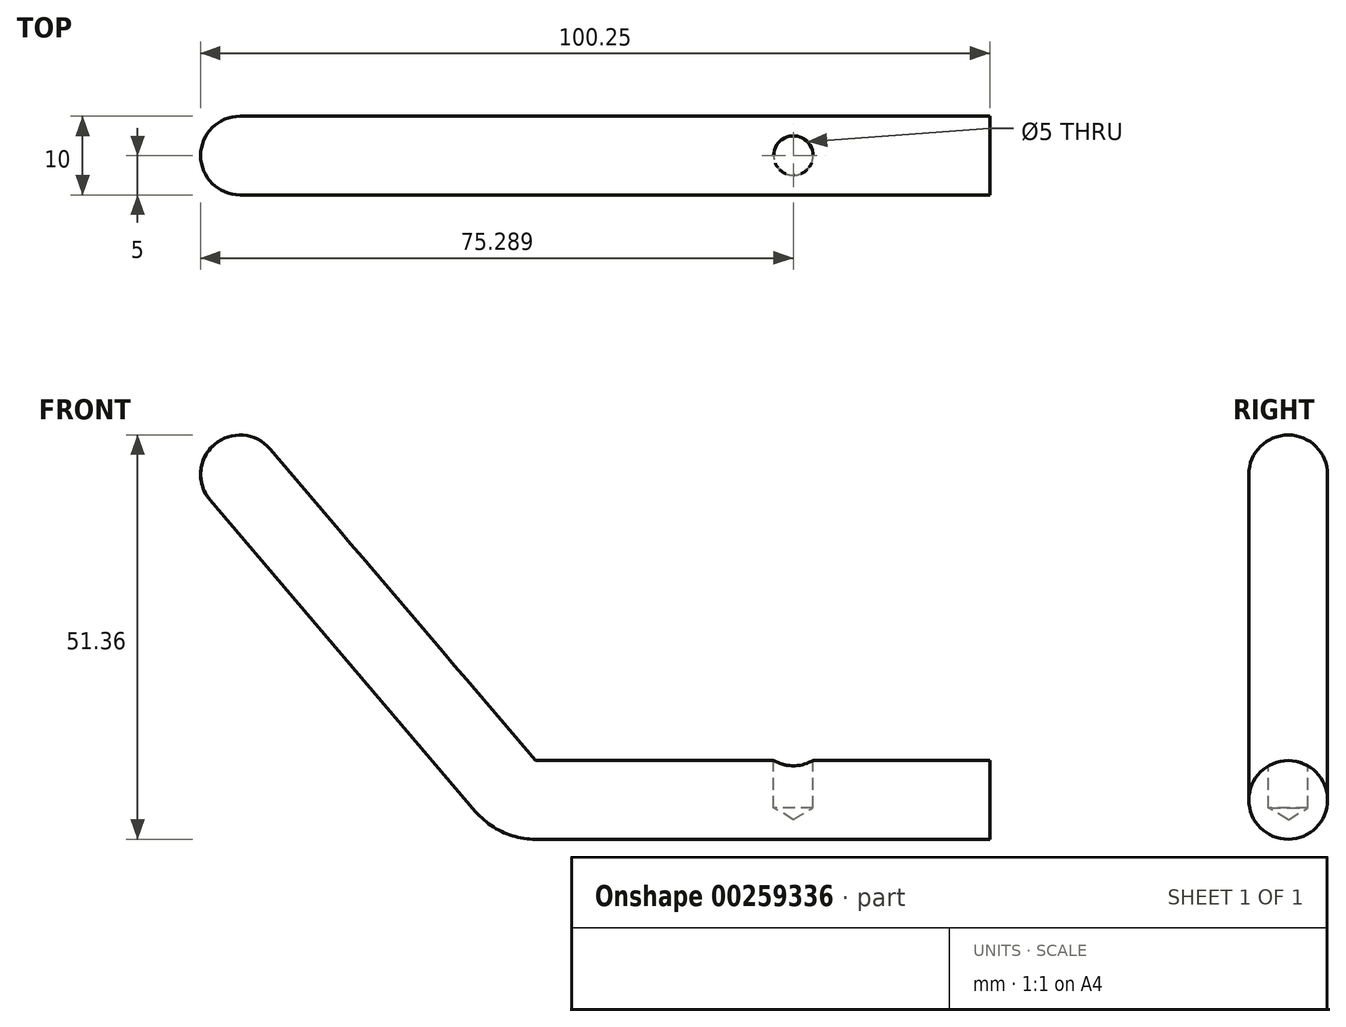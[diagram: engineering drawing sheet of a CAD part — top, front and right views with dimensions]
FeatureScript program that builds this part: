
annotation { "Feature Type Name" : "Feature", "Feature Type Description" : "" }
export const myFeature = defineFeature(function(context is Context, id is Id, definition is map)
    precondition{}
    {
        {
            var Q0;
            Q0=qCreatedBy(makeId("Front.planeOp"),FACE);
            var sketch = newSketch(context, id + "F0", { "sketchPlane" : qUnion([Q0])});
            skLineSegment(sketch, "E0", {"start": v(2.3, 0) * mm, "end": v(112.12, 0) * mm, "construction": true});
            skLineSegment(sketch, "E1", {"start": v(60, 5) * mm, "end": v(60, 0) * mm});
            skPoint(sketch, "E1.endSnap0", {"position": v(56.06, 0) * mm});
            skLineSegment(sketch, "E2", {"start": v(60, 0) * mm, "end": v(2.3, 0) * mm});
            skLineSegment(sketch, "E3", {"start": v(-53.4, 62.64) * mm, "end": v(-1.5, 1.76) * mm});
            skPoint(sketch, "E4.visualSharp", {"position": v(0, 5) * mm});
            skPoint(sketch, "E5.visualSharp", {"position": v(0, 0) * mm});
            skArc(sketch, "E5.filletArc", {"start": v(-1.5, 1.76) * mm, "mid": v(0.21, 0.46) * mm, "end": v(2.3, 0) * mm});
            skLineSegment(sketch, "E6.MirrorCS", {"start": v(-38.5, 45.16) * mm, "end": v(-1.5, 1.76) * mm});
            skPoint(sketch, "E7.visualSharp", {"position": v(2.4, 5) * mm});
            skLineSegment(sketch, "E8", {"start": v(-38.5, 45.16) * mm, "end": v(-61.75, 72.33) * mm, "construction": true});
            skArc(sketch, "E9", {"start": v(-50.24, 58.88) * mm, "mid": v(-50.23, 58.9) * mm, "end": v(-50.21, 58.9) * mm});
            skLineSegment(sketch, "E10", {"start": v(-53.4, 62.64) * mm, "end": v(-56.62, 66.33) * mm});
            skSolve(sketch);
        }
        {
            var Q0;
            Q0=qCreatedBy(makeId("Right.planeOp"),FACE);
            cPlane(context, id + "F1", {"entities" : qUnion([Q0]), "cplaneType" : CPlaneType.OFFSET, "offset" : 60 * mm, "width" : 150 * mm, "height" : 150 * mm});
        }
        {
            var Q0;
            Q0=qCreatedBy(id+"F1.planeOp",FACE);
            var sketch = newSketch(context, id + "F2", { "sketchPlane" : qUnion([Q0])});
            skCircle(sketch, "E11", {"center": v(0, 0) * mm, "radius": 5 * mm});
            skSolve(sketch);
        }
        {
            var Q0;
            Q0=makeQuery(id+"F2.imprint","IMPRINT",FACE,{"disambiguationData":[TD([[makeQuery(id+"F2.imprint","IMPRINT",EDGE,{"derivedFrom":sQuery(id+"F2.wireOp",EDGE,"E11")}),1.0]])]});
            var Q1;
            Q1=sQuery(id+"F0.wireOp",EDGE,"E2");
            var Q2;
            Q2=sQuery(id+"F0.wireOp",EDGE,"E5.filletArc");
            var Q3;
            Q3=sQuery(id+"F0.wireOp",EDGE,"E6.MirrorCS");
            sweep(context, id + "F3", {"profiles" : qUnion([Q0]), "path" : qUnion([Q1, Q2, Q3])});
        }
        {
            var Q0;
            Q0=qCreatedBy(id+"F1.planeOp",FACE);
            cPlane(context, id + "F4", {"entities" : qUnion([Q0]), "cplaneType" : CPlaneType.OFFSET, "offset" : 25 * mm, "oppositeDirection" : true, "width" : 150 * mm, "height" : 150 * mm});
        }
        {
            var Q0;
            Q0=qCreatedBy(makeId("Top.planeOp"),FACE);
            cPlane(context, id + "F5", {"entities" : qUnion([Q0]), "cplaneType" : CPlaneType.OFFSET, "offset" : 5 * mm, "width" : 150 * mm, "height" : 150 * mm});
        }
        {
            var Q0;
            Q0=qCreatedBy(id+"F5.planeOp",FACE);
            var sketch = newSketch(context, id + "F6", { "sketchPlane" : qUnion([Q0])});
            skCircle(sketch, "E12", {"center": v(35.04, 0) * mm, "radius": 3.21 * mm, "construction": true});
            skLineSegment(sketch, "E13", {"start": v(35.04, 0) * mm, "end": v(35.04, -4.5) * mm, "construction": true});
            skLineSegment(sketch, "E14", {"start": v(35.04, 0) * mm, "end": v(38.62, 0) * mm, "construction": true});
            skSolve(sketch);
        }
        {
            var Q0;
            Q0=sQuery(id+"F6.wireOp",VERTEX,"E12.center");
            var Q1;
            Q1=makeQuery(id+"F3.opSweep","SWEPT_BODY",BODY,{"disambiguationData":[OSD([sQuery(id+"F0.wireOp",EDGE,"E6.MirrorCS"),sQuery(id+"F2.wireOp",EDGE,"E11")])]});
            hole(context, id + "F7", {"style" : HoleStyle.SIMPLE, "endStyle" : HoleEndStyle.BLIND, "holeDiameter" : 5 * mm, "holeDepth" : 6 * mm, "tappedDepth" : 12 * mm, "tapClearance" : 3, "startFromSketch" : true, "locations" : qUnion([Q0]), "scope" : qUnion([Q1])});
        }
        {
            var Q0;
            Q0=makeQuery(id+"F3.opSweep","CAP_EDGE",EDGE,{"disambiguationData":[OSD([sQuery(id+"F0.wireOp",VERTEX,"E6.MirrorCS.start"),sQuery(id+"F2.wireOp",EDGE,"E11")])],"isStart":false});
            fillet(context, id + "F8", {"entities" : qUnion([Q0]), "radius" : 5 * mm, "tangentPropagation" : true, "allowEdgeOverflow" : false});
        }
    });
